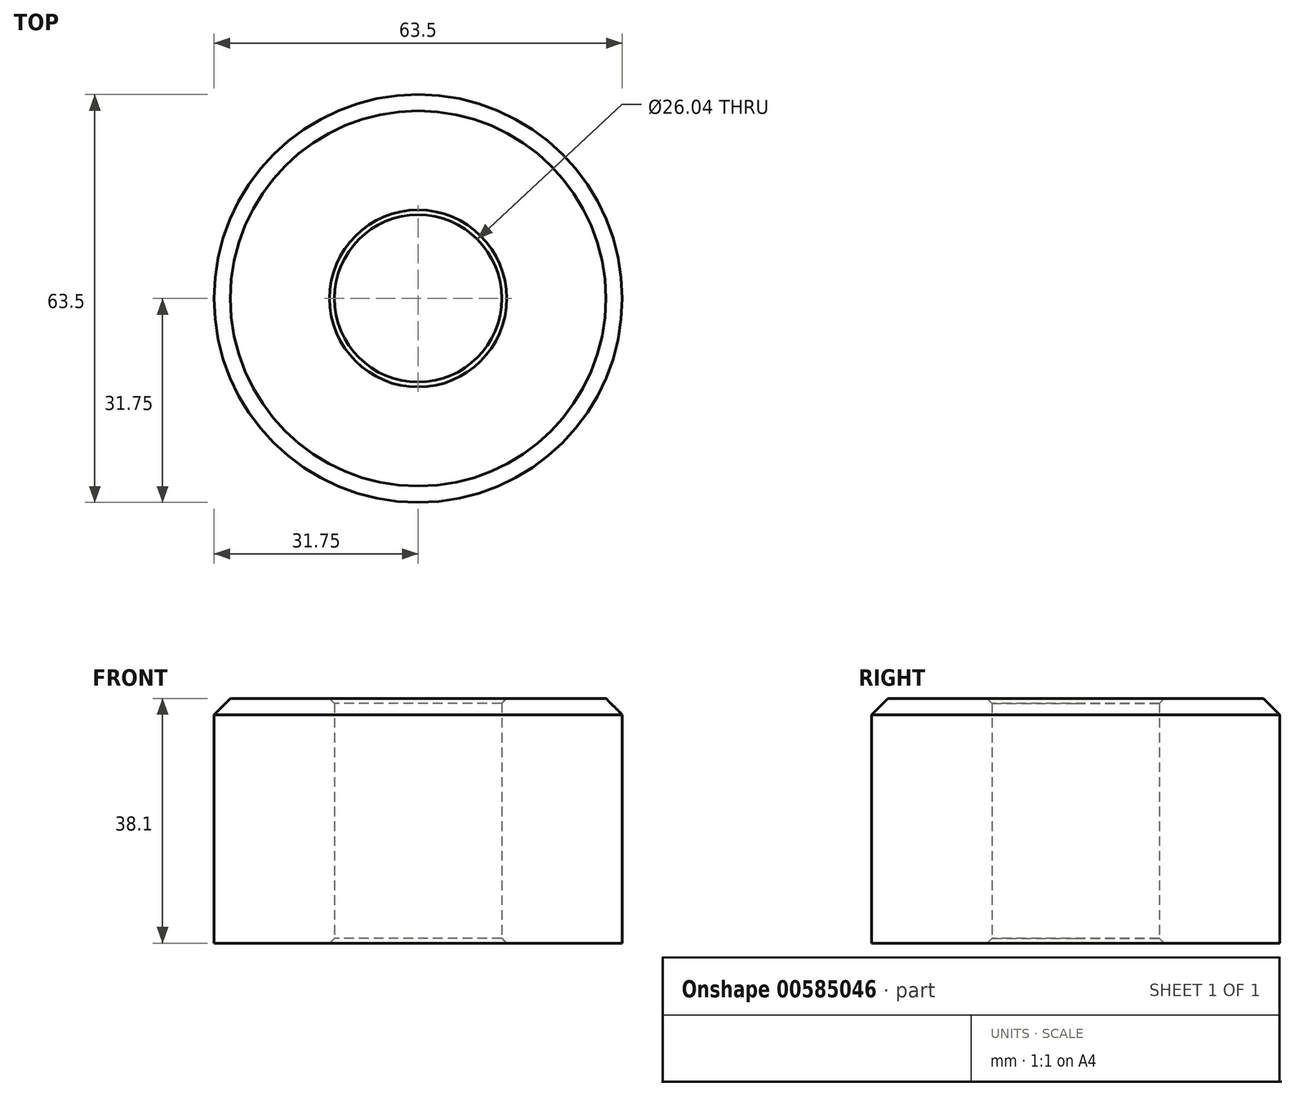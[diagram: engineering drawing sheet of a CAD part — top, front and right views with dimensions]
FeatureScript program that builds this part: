
annotation { "Feature Type Name" : "Feature", "Feature Type Description" : "" }
export const myFeature = defineFeature(function(context is Context, id is Id, definition is map)
    precondition{}
    {
        {
            var Q0;
            Q0=qCreatedBy(makeId("Top.planeOp"),FACE);
            var sketch = newSketch(context, id + "F0", { "sketchPlane" : qUnion([Q0])});
            skCircle(sketch, "E0", {"center": v(0, 0) * mm, "radius": 31.75 * mm});
            skCircle(sketch, "E1", {"center": v(0, 0) * mm, "radius": 13.02 * mm});
            skSolve(sketch);
        }
        {
            var Q0;
            Q0 = qSketchRegion(id + "F0", true);
            extrude(context, id + "F1", {"entities" : qUnion([Q0]), "depth" : 38.1 * mm, "offsetDistance" : 25.4 * mm});
        }
        {
            var Q0;
            Q0=makeQuery(id+"F1.opExtrude","CAP_EDGE",EDGE,{"disambiguationData":[OSD([sQuery(id+"F0.wireOp",EDGE,"E0")])],"isStart":false});
            chamfer(context, id + "F2", {"entities" : qUnion([Q0]), "width" : 2.54 * mm, "tangentPropagation" : true});
        }
        {
            var Q0;
            Q0=makeQuery(id+"F1.opExtrude","CAP_EDGE",EDGE,{"disambiguationData":[OSD([sQuery(id+"F0.wireOp",EDGE,"E1")])],"isStart":false});
            var Q1;
            Q1=makeQuery(id+"F1.opExtrude","CAP_EDGE",EDGE,{"disambiguationData":[OSD([sQuery(id+"F0.wireOp",EDGE,"E1")])],"isStart":true});
            chamfer(context, id + "F3", {"entities" : qUnion([Q0, Q1]), "width" : 0.76 * mm, "tangentPropagation" : true});
        }
    });
